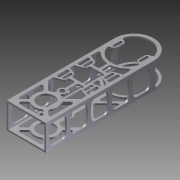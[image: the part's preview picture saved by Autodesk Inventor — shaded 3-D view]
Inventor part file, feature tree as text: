
AUTODESK INVENTOR PART (.ipt)
format: ipt  version: 2012 (Build 160160000, 160)  size: 822,272 bytes
history: native  units: in
note: dims shown in document units (in); Inventor stores cm internally (conversion verified against a paired STEP export)
features: extrude x6, sketch x5, fillet x3
ambient origin geometry x8: Origin, YZ Plane, XZ Plane, XY Plane, X Axis, Y Axis, Z Axis, Center Point
bodies: Solid1 (feature_tree)
feature tree (14):
  extrude  "Extrusion1"  Depth=3.0in
  sketch  "Sketch2"  dims[d2=0.125in d3=0.125in d4=0.125in]
  extrude  "Extrusion2"  Depth=0.125in
  fillet  "Fillet1"  Radius=0.125in
  sketch  "Sketch3"  dims[d5=0.125in d6=10.0in d7=0.0in]
  extrude  "Extrusion3"  Depth=10.0in TaperAngle=0.0deg
  extrude  "Extrusion4"  Depth=1.5in
  fillet  "Fillet2"  Radius=1.5in
  extrude  "Extrusion5"  Depth=1.5in
  fillet  "Fillet3"  Radius=2.25in
  extrude  "Extrusion6"  Depth=0.5in
  sketch  "Sketch1"  dims[d0=2.0in d1=3.0in]
  sketch  "Sketch4"  dims[d8=1.25in d9=1.5in d10=1.5in]
  sketch  "Sketch5"  dims[d11=1.3125in d15=1.5in d16=2.25in d18=0.5in d30=0.366in d31=1.75in d32=0.125in d33=0.125in d34=0.125in d35=0.125in d36=0.125in d37=0.125in d38=0.25in d39=0.25in d41=0.25in d42=0.875in d43=1.5in d44=0.125in d45=0.125in d46=0.125in d47=0.125in d48=0.3125in d49=0.25in d50=0.0in d51=0.125in d52=0.5in d53=0.1in d54=0.5in d55=0.1in d56=0.5in d57=0.1in d58=0.5in d59=0.1in d60=1.6in d61=1.6in d62=0.5in d63=0.5in d64=0.8in d65=0.8in d66=3.0in d70=0.1in d71=2.0in d74=2.0in d75=2.5in d76=0.2in d77=0.2in d78=1.5in d79=0.25in d80=0.25in d81=0.25in d82=0.25in d83=0.1in d84=1.0in d85=0.0in d86=0.5in d87=0.5in d89=1.0in d90=7.75in d91=2.5in d92=0.366in d94=0.125in d95=0.125in d96=0.875in d97=0.25in d98=0.25in d99=0.25in d100=0.125in d101=0.125in d102=0.25in d103=0.2in d106=0.1875in d107=0.0938in d108=0.1875in d109=0.0938in d110=0.0938in d111=0.1875in d112=0.3in d113=0.125in d114=0.481in d115=0.481in d116=0.2in d119=1.4375in d120=0.1875in d121=0.0938in d123=1.2in d124=0.481in d125=0.481in d126=0.125in d127=0.0in d128=0.125in d129=0.125in d130=0.125in d131=0.125in d132=0.625in d133=0.375in d172=0.125in d173=0.0in d174=0.25in d175=0.25in d176=0.25in d177=0.25in d178=0.25in d179=3.0in d181=0.125in d183=0.125in d184=1.6in d185=1.9685in d187=1.6in d188=0.3937in d190=1.0in d192=0.125in d193=0.125in d194=0.125in d195=0.125in d196=0.125in d197=0.125in d198=0.125in d199=0.125in d200=0.481in d201=1.25in d202=5.0in d203=45.0deg d204=0.0938in d205=0.1875in d206=0.1875in d209=0.0625in d210=0.0in]
